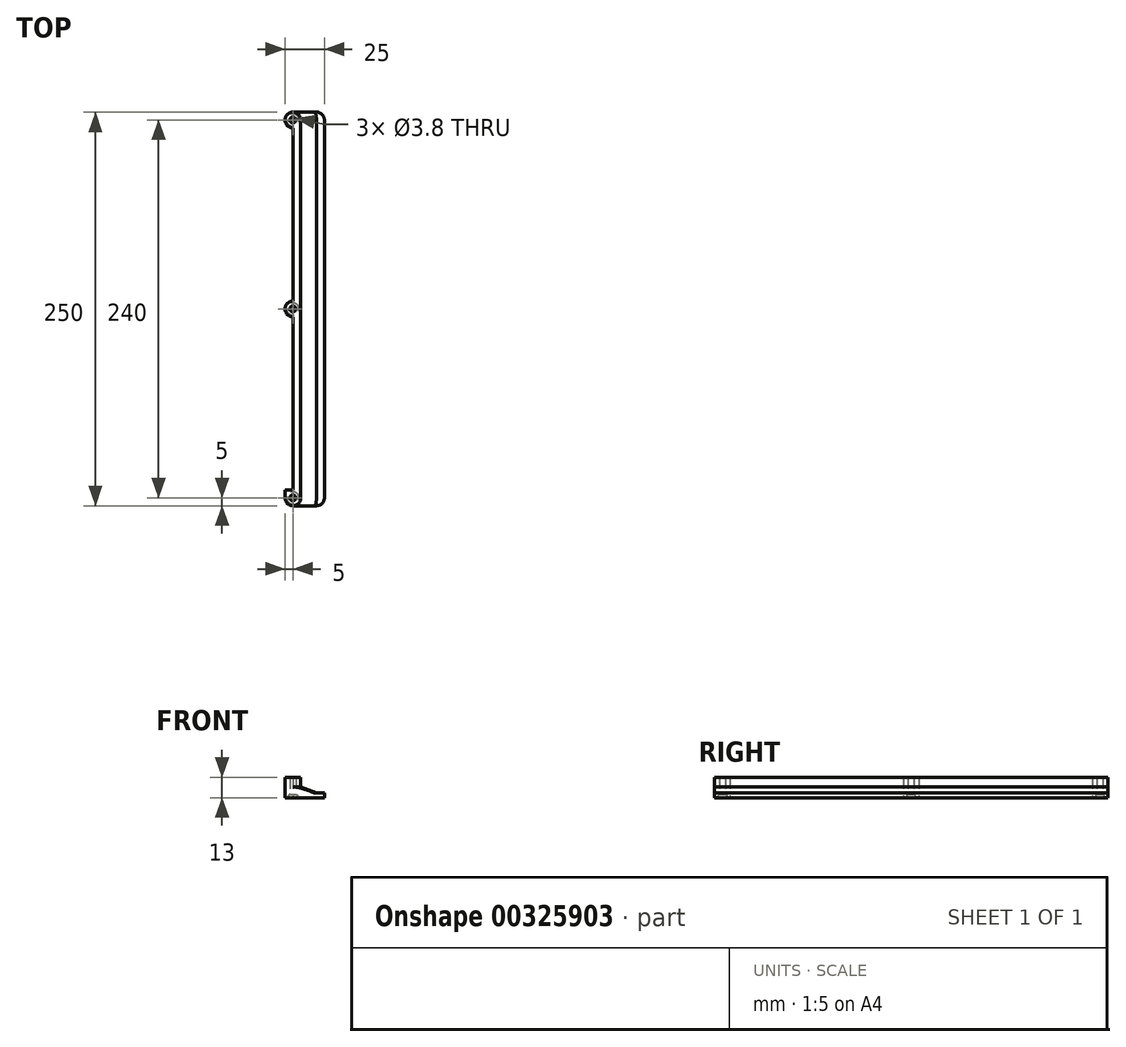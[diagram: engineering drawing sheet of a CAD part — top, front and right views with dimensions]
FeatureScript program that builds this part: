
annotation { "Feature Type Name" : "Feature", "Feature Type Description" : "" }
export const myFeature = defineFeature(function(context is Context, id is Id, definition is map)
    precondition{}
    {
        {
            var Q0;
            Q0=qCreatedBy(makeId("Front.planeOp"),FACE);
            var sketch = newSketch(context, id + "F0", { "sketchPlane" : qUnion([Q0])});
            skLineSegment(sketch, "E0", {"start": v(-25, 13) * mm, "end": v(-25, 0) * mm});
            skLineSegment(sketch, "E1", {"start": v(-25, 0) * mm, "end": v(0, 0) * mm});
            skLineSegment(sketch, "E2", {"start": v(0, 0) * mm, "end": v(0, 3) * mm});
            skLineSegment(sketch, "E3", {"start": v(0, 3) * mm, "end": v(-15, 3) * mm});
            skLineSegment(sketch, "E4", {"start": v(-15, 3) * mm, "end": v(-15, 13) * mm});
            skLineSegment(sketch, "E5", {"start": v(-15, 13) * mm, "end": v(-25, 13) * mm});
            skSolve(sketch);
        }
        {
            var Q0;
            Q0=makeQuery(id+"F0.imprint","IMPRINT",FACE,{"disambiguationData":[TD([[makeQuery(id+"F0.imprint","IMPRINT",EDGE,{"derivedFrom":sQuery(id+"F0.wireOp",EDGE,"E0")}),1.0]])]});
            extrude(context, id + "F1", {"entities" : qUnion([Q0]), "depth" : 250 * mm});
        }
        {
            var Q0;
            Q0=makeQuery(id+"F1.opExtrude","SWEPT_FACE",FACE,{"disambiguationData":[OSD([sQuery(id+"F0.wireOp",EDGE,"E1")])]});
            var sketch = newSketch(context, id + "F2", { "sketchPlane" : qUnion([Q0])});
            skLineSegment(sketch, "E6.0", {"start": v(-25, 250) * mm, "end": v(-25, 0) * mm});
            skLineSegment(sketch, "E6.1", {"start": v(-15, 250) * mm, "end": v(-25, 250) * mm});
            skLineSegment(sketch, "E6.2", {"start": v(-15, 250) * mm, "end": v(-15, 0) * mm});
            skLineSegment(sketch, "E6.3", {"start": v(-15, 0) * mm, "end": v(-25, 0) * mm});
            skPoint(sketch, "E7", {"position": v(-20, 245) * mm});
            skPoint(sketch, "E7.positionSnap0", {"position": v(-20, 250) * mm});
            skPoint(sketch, "E8", {"position": v(-20, 5) * mm});
            skPoint(sketch, "E8.positionSnap0", {"position": v(-20, 0) * mm});
            skPoint(sketch, "E9", {"position": v(-20, 125) * mm});
            skPoint(sketch, "E9.positionSnap0", {"position": v(-15, 125) * mm});
            skLineSegment(sketch, "E10", {"start": v(-25, 240) * mm, "end": v(-15, 240) * mm});
            skLineSegment(sketch, "E11", {"start": v(-25, 130) * mm, "end": v(-15, 130) * mm});
            skLineSegment(sketch, "E12", {"start": v(-25, 120) * mm, "end": v(-15, 120) * mm});
            skLineSegment(sketch, "E13", {"start": v(-25, 10) * mm, "end": v(-15, 10) * mm});
            skLineSegment(sketch, "E14", {"start": v(-20, 250) * mm, "end": v(-20, 0) * mm});
            skSolve(sketch);
        }
        {
            var Q0;
            Q0=sQuery(id+"F2.wireOp",VERTEX,"E7");
            var Q1;
            Q1=sQuery(id+"F2.wireOp",VERTEX,"E9");
            var Q2;
            Q2=sQuery(id+"F2.wireOp",VERTEX,"E8");
            var Q3;
            Q3=makeQuery(id+"F1.opExtrude","SWEPT_BODY",BODY,{"disambiguationData":[OSD([sQuery(id+"F0.wireOp",EDGE,"E0"),sQuery(id+"F0.wireOp",EDGE,"E1"),sQuery(id+"F0.wireOp",EDGE,"E2"),sQuery(id+"F0.wireOp",EDGE,"E3"),sQuery(id+"F0.wireOp",EDGE,"E4"),sQuery(id+"F0.wireOp",EDGE,"E5")])]});
            hole(context, id + "F3", {"style" : HoleStyle.C_SINK, "endStyle" : HoleEndStyle.THROUGH, "standardTappedOrClearance" : lookupTablePath({ "standard" : "ANSI", "fit" : "Normal (ASME)", "size" : "#6", "type" : "Clearance" }), "standardBlindInLast" : lookupTablePath({ "fit" : "Free", "standard" : "ANSI", "size" : "#6", "type" : "Clearance" }), "holeDiameter" : 3.8 * mm, "cSinkDiameter" : 7.8 * mm, "cSinkAngle" : 82 * degree, "tappedDepth" : 12 * mm, "tapClearance" : 3, "startFromSketch" : true, "locations" : qUnion([Q0, Q1, Q2]), "scope" : qUnion([Q3])});
        }
        {
            var Q0;
            {var subQ0=sQuery(id+"F2.wireOp",EDGE,"E10");var subQ1=sQuery(id+"F2.wireOp",EDGE,"E6.0");var subQ2=makeQuery(id+"F2.imprint","INTERSECT",VERTEX,{"derivedFrom":[subQ1,subQ0]});Q0=makeQuery(id+"F2.imprint","IMPRINT",FACE,{"disambiguationData":[TD([[makeQuery(id+"F2.imprint","IMPRINT",EDGE,{"disambiguationData":[TD([[subQ2,-1.0]])],"derivedFrom":subQ1}),1.0]])]});}
            var Q1;
            {var subQ0=sQuery(id+"F2.wireOp",EDGE,"E12");var subQ1=sQuery(id+"F2.wireOp",EDGE,"E6.0");var subQ2=makeQuery(id+"F2.imprint","INTERSECT",VERTEX,{"derivedFrom":[subQ1,subQ0]});Q1=makeQuery(id+"F2.imprint","IMPRINT",FACE,{"disambiguationData":[TD([[makeQuery(id+"F2.imprint","IMPRINT",EDGE,{"disambiguationData":[TD([[subQ2,-1.0]])],"derivedFrom":subQ1}),1.0]])]});}
            extrude(context, id + "F4", {"entities" : qUnion([Q0, Q1]), "operationType" : NewBodyOperationType.REMOVE, "endBound" : BoundingType.THROUGH_ALL, "oppositeDirection" : true, "depth" : 25 * mm});
        }
        {
            var Q0;
            Q0=makeQuery(id+"F1.opExtrude","CAP_EDGE",EDGE,{"disambiguationData":[OSD([sQuery(id+"F0.wireOp",EDGE,"E0")])],"isStart":true});
            var Q1;
            Q1=makeQuery(id+"F4.boolean.opBoolean","COPY",EDGE,{"derivedFrom":makeQuery(id+"F4.opExtrude","SWEPT_EDGE",EDGE,{"disambiguationData":[OSD([sQuery(id+"F2.wireOp",EDGE,"E6.0"),sQuery(id+"F2.wireOp",EDGE,"E13")])]})});
            var Q2;
            Q2=makeQuery(id+"F4.boolean.opBoolean","COPY",EDGE,{"derivedFrom":makeQuery(id+"F4.opExtrude","SWEPT_EDGE",EDGE,{"disambiguationData":[OSD([sQuery(id+"F2.wireOp",EDGE,"E6.0"),sQuery(id+"F2.wireOp",EDGE,"E12")])]})});
            var Q3;
            Q3=makeQuery(id+"F4.boolean.opBoolean","COPY",EDGE,{"derivedFrom":makeQuery(id+"F4.opExtrude","SWEPT_EDGE",EDGE,{"disambiguationData":[OSD([sQuery(id+"F2.wireOp",EDGE,"E6.0"),sQuery(id+"F2.wireOp",EDGE,"E11")])]})});
            var Q4;
            Q4=makeQuery(id+"F4.boolean.opBoolean","COPY",EDGE,{"derivedFrom":makeQuery(id+"F4.opExtrude","SWEPT_EDGE",EDGE,{"disambiguationData":[OSD([sQuery(id+"F2.wireOp",EDGE,"E6.0"),sQuery(id+"F2.wireOp",EDGE,"E10")])]})});
            var Q5;
            Q5=makeQuery(id+"F1.opExtrude","CAP_EDGE",EDGE,{"disambiguationData":[OSD([sQuery(id+"F0.wireOp",EDGE,"E0")])],"isStart":false});
            var Q6;
            Q6=makeQuery(id+"F1.opExtrude","CAP_EDGE",EDGE,{"disambiguationData":[OSD([sQuery(id+"F0.wireOp",EDGE,"E4")])],"isStart":false});
            var Q7;
            Q7=makeQuery(id+"F1.opExtrude","CAP_EDGE",EDGE,{"disambiguationData":[OSD([sQuery(id+"F0.wireOp",EDGE,"E2")])],"isStart":false});
            var Q8;
            Q8=makeQuery(id+"F1.opExtrude","CAP_EDGE",EDGE,{"disambiguationData":[OSD([sQuery(id+"F0.wireOp",EDGE,"E4")])],"isStart":true});
            var Q9;
            Q9=makeQuery(id+"F1.opExtrude","CAP_EDGE",EDGE,{"disambiguationData":[OSD([sQuery(id+"F0.wireOp",EDGE,"E2")])],"isStart":true});
            fillet(context, id + "F5", {"entities" : qUnion([Q0, Q1, Q2, Q3, Q4, Q5, Q6, Q7, Q8, Q9]), "radius" : 5 * mm, "tangentPropagation" : true, "allowEdgeOverflow" : false});
        }
        {
            var Q0;
            Q0=makeQuery(id+"F1.opExtrude","SWEPT_EDGE",EDGE,{"disambiguationData":[OSD([sQuery(id+"F0.wireOp",EDGE,"E3"),sQuery(id+"F0.wireOp",EDGE,"E4")])]});
            chamfer(context, id + "F6", {"entities" : qUnion([Q0]), "chamferType" : ChamferType.TWO_OFFSETS, "width1" : 4 * mm, "oppositeDirection" : false, "width2" : 10 * mm, "tangentPropagation" : true});
        }
    });
